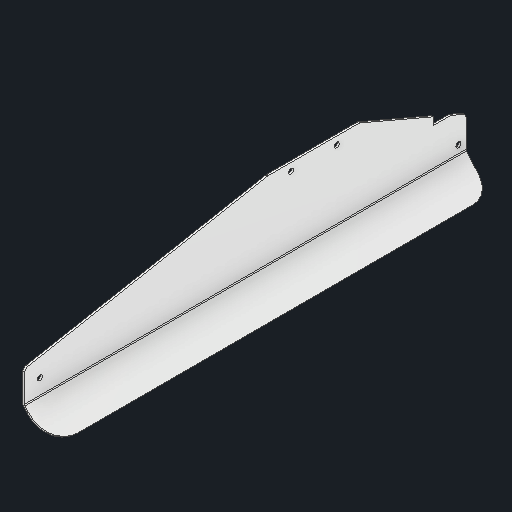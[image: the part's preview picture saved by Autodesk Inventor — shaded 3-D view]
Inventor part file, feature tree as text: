
AUTODESK INVENTOR PART (.ipt)
format: ipt  version: 2025 (Build 290162000, 162)  size: 144,896 bytes
history: native  units: in
note: dims shown in document units (in); Inventor stores cm internally (conversion verified against a paired STEP export)
features: other x4, sketch x1, extrude x1
ambient origin geometry x8: Origin, YZ Plane, XZ Plane, XY Plane, X Axis, Y Axis, Z Axis, Center Point
bodies: Solid1 (feature_tree)
feature tree (6):
  other  "Blocks"
  sketch  "Sketch1"  dims[d0=1.0in d1=0.125in d2=0.125in d3=0.125in d4=1.25in d5=90.0deg d6=1.0in d7=0.5in d8=0.0625in d9=0.0in d10=0.125in d11=0.2749in d16=0.5in d17=0.5625in]
  extrude  "Extrusion1"  Depth=0.0625in TaperAngle=0.0deg
  other  "Bend Part1"
  other  "main"
  other  "main:1"
